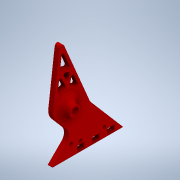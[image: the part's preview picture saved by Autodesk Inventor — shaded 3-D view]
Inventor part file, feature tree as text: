
AUTODESK INVENTOR PART (.ipt)
format: ipt  version: 2020 (Build 240168000, 168)  size: 318,976 bytes
history: native  units: mm
features: extrude x7, sketch x7, other x3, fillet x1, chamfer x1, projected_geometry x1
ambient origin geometry x8: Origin, YZ Plane, XZ Plane, XY Plane, X Axis, Y Axis, Z Axis, Center Point
bodies: Solid1 (feature_tree)
feature tree (20):
  other  "WeaponMountBasePlateV1.ipt"
  extrude  "Extrusion1"  Depth=10.0mm
  extrude  "Extrusion2"  TaperAngle=0.0deg  [1 undecoded]
  extrude  "Extrusion3"  Depth=0.75mm
  fillet  "Fillet2"  [1 undecoded]
  extrude  "Extrusion4"  Depth=1.9mm
  extrude  "Extrusion5"  Depth=8.0mm
  extrude  "Extrusion6"  Depth=10.0mm TaperAngle=0.0deg
  chamfer  "Chamfer1"  [1 undecoded]
  extrude  "Extrusion7"  Depth=2.0mm
  other  "Solid1::WeaponMountBasePlateV1.ipt"
  other  "TaggingFeature1"
  sketch  "Sketch2"  dims[d0=10.0mm d2=11.3mm]
  sketch  "Sketch3"  dims[d3=10.0mm d4=0.0mm]
  sketch  "Sketch4"  dims[d5=7.3mm d6=0.75mm d7=0.0mm]
  projected_geometry  "Projected Loop1"
  sketch  "Sketch5"  dims[d8=7.3mm d9=1.9mm]
  sketch  "Sketch6"  dims[d10=0.0mm d12=8.0mm]
  sketch  "Sketch7"  dims[d13=4.5mm d14=10.0mm d15=0.0mm]
  sketch  "Sketch8"  dims[d16=2.2mm d17=0.0mm d18=0.0mm d19=4.0mm d20=2.0mm d21=0.0mm d22=0.9mm d23=2.0mm d24=45.0deg d25=6.1mm d26=0.0mm d27=-7.853982mm]
note: 3 required parameter values undecoded (feature->parameter linkage not recoverable at this tier; creation-order binding heuristic only, values carry confidence <= 0.55)
